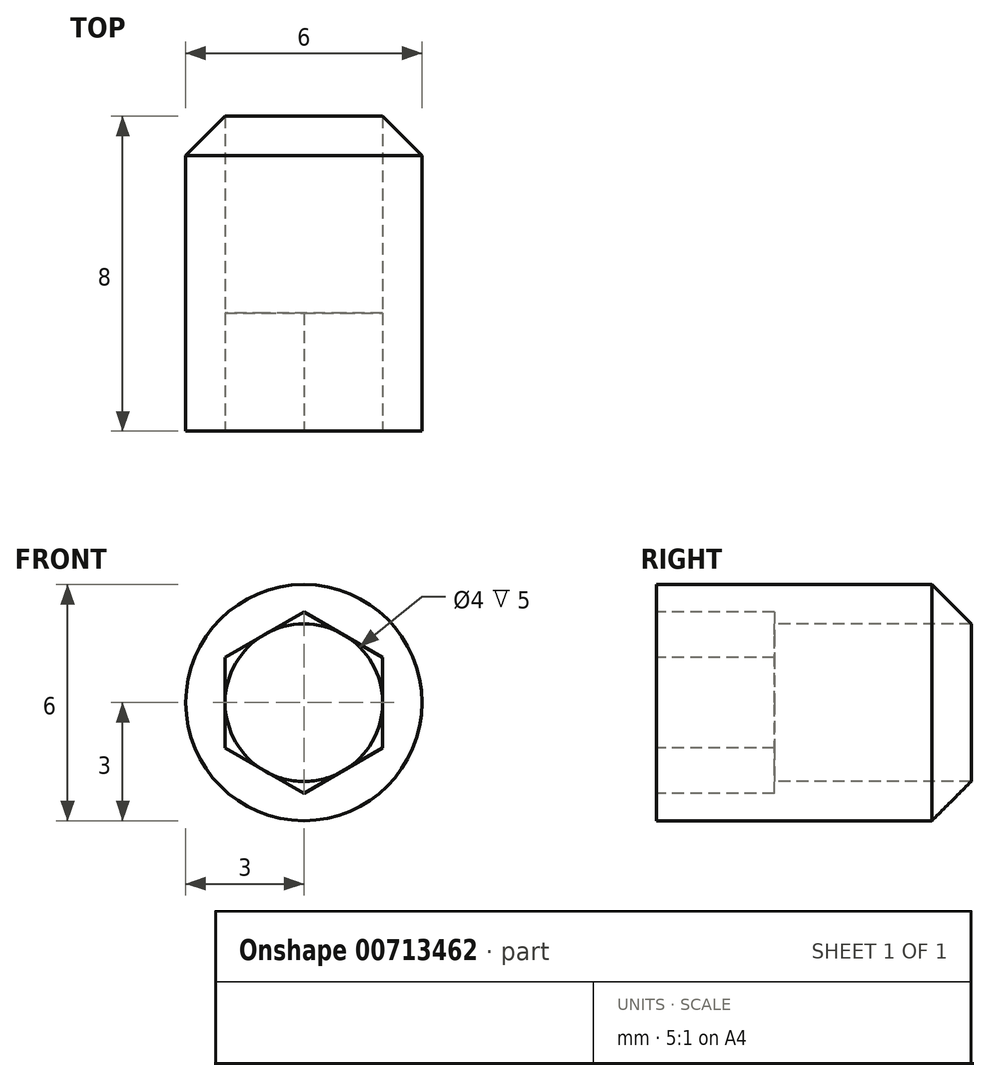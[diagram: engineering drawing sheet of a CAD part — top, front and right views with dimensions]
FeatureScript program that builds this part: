
annotation { "Feature Type Name" : "Feature", "Feature Type Description" : "" }
export const myFeature = defineFeature(function(context is Context, id is Id, definition is map)
    precondition{}
    {
        {
            var Q0;
            Q0=qCreatedBy(makeId("Front.planeOp"),FACE);
            var sketch = newSketch(context, id + "F0", { "sketchPlane" : qUnion([Q0])});
            skCircle(sketch, "E0", {"center": v(0, 0) * mm, "radius": 3 * mm});
            skSolve(sketch);
        }
        {
            var Q0;
            Q0 = qSketchRegion(id + "F0", true);
            extrude(context, id + "F1", {"entities" : qUnion([Q0]), "depth" : 8 * mm, "offsetDistance" : 25 * mm});
        }
        {
            var Q0;
            Q0=makeQuery(id+"F1.opExtrude","CAP_FACE",FACE,{"disambiguationData":[OSD([sQuery(id+"F0.wireOp",EDGE,"E0")])],"isStart":false});
            var sketch = newSketch(context, id + "F2", { "sketchPlane" : qUnion([Q0])});
            skCircle(sketch, "E1.cCircle", {"center": v(0, 0) * mm, "radius": 2 * mm, "construction": true});
            skLineSegment(sketch, "E1.0", {"start": v(0, 2.3) * mm, "end": v(2, 1.15) * mm});
            skLineSegment(sketch, "E1.1", {"start": v(2, 1.15) * mm, "end": v(2, -1.15) * mm});
            skLineSegment(sketch, "E1.2", {"start": v(2, -1.15) * mm, "end": v(0, -2.3) * mm});
            skLineSegment(sketch, "E1.3", {"start": v(0, -2.3) * mm, "end": v(-2, -1.15) * mm});
            skLineSegment(sketch, "E1.4", {"start": v(-2, -1.15) * mm, "end": v(-2, 1.15) * mm});
            skLineSegment(sketch, "E1.5", {"start": v(-2, 1.15) * mm, "end": v(0, 2.3) * mm});
            skPoint(sketch, "E1.0.midPoint", {"position": v(1, 1.73) * mm});
            skSolve(sketch);
        }
        {
            var Q0;
            Q0 = qSketchRegion(id + "F2", true);
            extrude(context, id + "F3", {"entities" : qUnion([Q0]), "operationType" : NewBodyOperationType.REMOVE, "oppositeDirection" : true, "depth" : 3 * mm, "offsetDistance" : 25 * mm});
        }
        {
            var Q0;
            Q0=makeQuery(id+"F3.boolean.opBoolean","COPY",FACE,{"derivedFrom":makeQuery(id+"F3.opExtrude","CAP_FACE",FACE,{"disambiguationData":[OSD([sQuery(id+"F2.wireOp",EDGE,"E1.0"),sQuery(id+"F2.wireOp",EDGE,"E1.1"),sQuery(id+"F2.wireOp",EDGE,"E1.2"),sQuery(id+"F2.wireOp",EDGE,"E1.3"),sQuery(id+"F2.wireOp",EDGE,"E1.4"),sQuery(id+"F2.wireOp",EDGE,"E1.5")])],"isStart":false})});
            var sketch = newSketch(context, id + "F4", { "sketchPlane" : qUnion([Q0])});
            skCircle(sketch, "E2", {"center": v(0, 0) * mm, "radius": 2 * mm});
            skSolve(sketch);
        }
        {
            var Q0;
            Q0 = qSketchRegion(id + "F4", true);
            extrude(context, id + "F5", {"entities" : qUnion([Q0]), "operationType" : NewBodyOperationType.REMOVE, "oppositeDirection" : true, "depth" : 25 * mm, "offsetDistance" : 25 * mm});
        }
        {
            var Q0;
            Q0=makeQuery(id+"F1.opExtrude","CAP_EDGE",EDGE,{"disambiguationData":[OSD([sQuery(id+"F0.wireOp",EDGE,"E0")])],"isStart":true});
            chamfer(context, id + "F6", {"entities" : qUnion([Q0]), "width" : 1 * mm, "tangentPropagation" : true});
        }
    });
